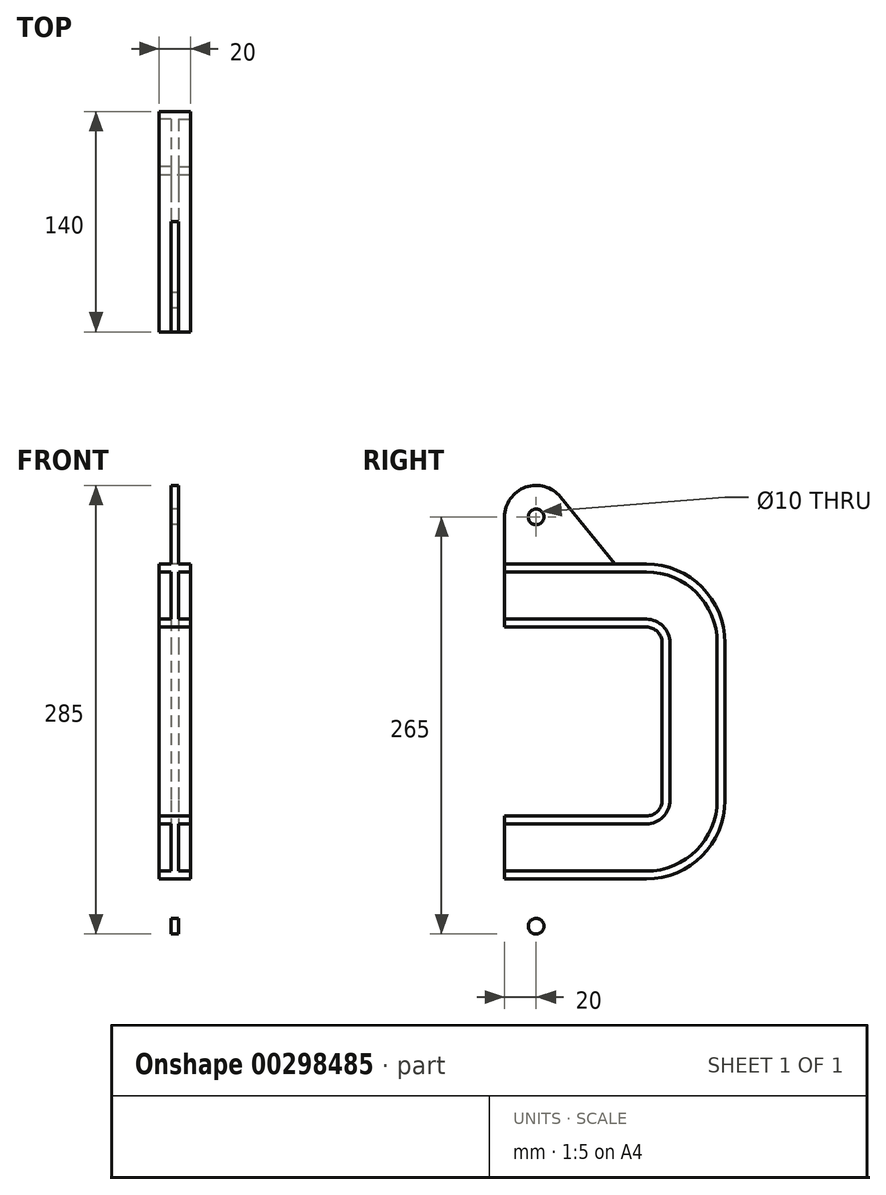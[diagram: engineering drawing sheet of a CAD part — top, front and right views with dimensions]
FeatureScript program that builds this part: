
annotation { "Feature Type Name" : "Feature", "Feature Type Description" : "" }
export const myFeature = defineFeature(function(context is Context, id is Id, definition is map)
    precondition{}
    {
        {
            var Q0;
            Q0=qCreatedBy(makeId("Front.planeOp"),FACE);
            var sketch = newSketch(context, id + "F0", { "sketchPlane" : qUnion([Q0])});
            skLineSegment(sketch, "E0", {"start": v(2.5, 0) * mm, "end": v(2.5, 15) * mm});
            skLineSegment(sketch, "E1", {"start": v(5.5, 15) * mm, "end": v(10, 15) * mm});
            skLineSegment(sketch, "E2", {"start": v(10, 15) * mm, "end": v(10, 20) * mm});
            skLineSegment(sketch, "E3", {"start": v(10, 20) * mm, "end": v(0, 20) * mm});
            skLineSegment(sketch, "E4.MirrorCS", {"start": v(-10, 15) * mm, "end": v(-10, 20) * mm});
            skLineSegment(sketch, "E5.MirrorCS", {"start": v(-2.5, 15) * mm, "end": v(-10, 15) * mm});
            skLineSegment(sketch, "E6.MirrorCS", {"start": v(-2.5, 0) * mm, "end": v(-2.5, 15) * mm});
            skLineSegment(sketch, "E7.MirrorCS", {"start": v(-10, 20) * mm, "end": v(0, 20) * mm});
            skLineSegment(sketch, "E8.MirrorCS", {"start": v(2.5, 0) * mm, "end": v(2.5, 12) * mm});
            skLineSegment(sketch, "E9.MirrorCS", {"start": v(-5.5, 15) * mm, "end": v(-10, 15) * mm});
            skLineSegment(sketch, "E10.MirrorCS", {"start": v(-2.5, 0) * mm, "end": v(-2.5, 12) * mm});
            skLineSegment(sketch, "E11.MirrorCS", {"start": v(2.5, 15) * mm, "end": v(10, 15) * mm});
            skLineSegment(sketch, "E12.MirrorCS", {"start": v(-10, -20) * mm, "end": v(0, -20) * mm});
            skLineSegment(sketch, "E13.MirrorCS", {"start": v(2.5, 0) * mm, "end": v(2.5, -15) * mm});
            skLineSegment(sketch, "E14.MirrorCS", {"start": v(5.5, -15) * mm, "end": v(10, -15) * mm});
            skLineSegment(sketch, "E15.MirrorCS", {"start": v(10, -15) * mm, "end": v(10, -20) * mm});
            skLineSegment(sketch, "E16.MirrorCS", {"start": v(-10, -15) * mm, "end": v(-10, -20) * mm});
            skLineSegment(sketch, "E17.MirrorCS", {"start": v(-2.5, 0) * mm, "end": v(-2.5, -15) * mm});
            skLineSegment(sketch, "E18.MirrorCS", {"start": v(-2.5, -15) * mm, "end": v(-10, -15) * mm});
            skLineSegment(sketch, "E19.MirrorCS", {"start": v(10, -20) * mm, "end": v(0, -20) * mm});
            skLineSegment(sketch, "E20.MirrorCS", {"start": v(2.5, -15) * mm, "end": v(10, -15) * mm});
            skLineSegment(sketch, "E21.MirrorCS", {"start": v(-2.5, 0) * mm, "end": v(-2.5, -12) * mm});
            skLineSegment(sketch, "E22.MirrorCS", {"start": v(-5.5, -15) * mm, "end": v(-10, -15) * mm});
            skLineSegment(sketch, "E23.MirrorCS", {"start": v(2.5, 0) * mm, "end": v(2.5, -12) * mm});
            skPoint(sketch, "E24.visualSharp", {"position": v(2.5, 15) * mm});
            skArc(sketch, "E24.filletArc", {"start": v(5.5, 15) * mm, "mid": v(3.38, 14.12) * mm, "end": v(2.5, 12) * mm});
            skPoint(sketch, "E25.visualSharp", {"position": v(-2.5, 15) * mm});
            skArc(sketch, "E25.filletArc", {"start": v(-2.5, 12) * mm, "mid": v(-3.38, 14.12) * mm, "end": v(-5.5, 15) * mm});
            skPoint(sketch, "E26.visualSharp", {"position": v(-2.5, -15) * mm});
            skArc(sketch, "E26.filletArc", {"start": v(-5.5, -15) * mm, "mid": v(-3.38, -14.12) * mm, "end": v(-2.5, -12) * mm});
            skPoint(sketch, "E27.visualSharp", {"position": v(2.5, -15) * mm});
            skArc(sketch, "E27.filletArc", {"start": v(2.5, -12) * mm, "mid": v(3.38, -14.12) * mm, "end": v(5.5, -15) * mm});
            skSolve(sketch);
        }
        {
            var Q0;
            Q0=qCreatedBy(makeId("Right.planeOp"),FACE);
            var sketch = newSketch(context, id + "F1", { "sketchPlane" : qUnion([Q0])});
            skLineSegment(sketch, "E28", {"start": v(0, -20) * mm, "end": v(90, -20) * mm});
            skLineSegment(sketch, "E29", {"start": v(100, -130) * mm, "end": v(100, -30) * mm});
            skLineSegment(sketch, "E30", {"start": v(90, -140) * mm, "end": v(0, -140) * mm});
            skPoint(sketch, "E31.visualSharp", {"position": v(100, -20) * mm});
            skArc(sketch, "E31.filletArc", {"start": v(100, -30) * mm, "mid": v(97.07, -22.93) * mm, "end": v(90, -20) * mm});
            skPoint(sketch, "E32.visualSharp", {"position": v(100, -140) * mm});
            skArc(sketch, "E32.filletArc", {"start": v(90, -140) * mm, "mid": v(97.07, -137.07) * mm, "end": v(100, -130) * mm});
            skSolve(sketch);
        }
        {
            var Q0;
            {var subQ4=sQuery(id+"F0.wireOp",EDGE,"E0");Q0=makeQuery(id+"F0.imprint","IMPRINT",FACE,{"disambiguationData":[TD([[makeQuery(id+"F0.imprint","IMPRINT",EDGE,{"derivedFrom":subQ4}),1.0]])]});}
            var Q1;
            Q1=sQuery(id+"F1.wireOp",EDGE,"E28");
            var Q2;
            Q2=sQuery(id+"F1.wireOp",EDGE,"E31.filletArc");
            var Q3;
            Q3=sQuery(id+"F1.wireOp",EDGE,"E29");
            var Q4;
            Q4=sQuery(id+"F1.wireOp",EDGE,"E32.filletArc");
            var Q5;
            Q5=sQuery(id+"F1.wireOp",EDGE,"E30");
            sweep(context, id + "F2", {"profiles" : qUnion([Q0]), "path" : qUnion([Q1, Q2, Q3, Q4, Q5])});
        }
        {
            var Q0;
            Q0=qCreatedBy(makeId("Right.planeOp"),FACE);
            var sketch = newSketch(context, id + "F3", { "sketchPlane" : qUnion([Q0])});
            skLineSegment(sketch, "E33", {"start": v(0, 20) * mm, "end": v(70, 20) * mm});
            skLineSegment(sketch, "E34", {"start": v(70, 20) * mm, "end": v(35.55, 62.58) * mm});
            skArc(sketch, "E35", {"start": v(35.55, 62.58) * mm, "mid": v(13.33, 68.85) * mm, "end": v(0, 50) * mm});
            skLineSegment(sketch, "E36", {"start": v(0, 50) * mm, "end": v(0, 20) * mm});
            skCircle(sketch, "E37", {"center": v(20, 50) * mm, "radius": 5 * mm});
            skLineSegment(sketch, "E38", {"start": v(33.98, -80) * mm, "end": v(186, -80) * mm, "construction": true});
            skCircle(sketch, "E39.MirrorC", {"center": v(20, -210) * mm, "radius": 5 * mm});
            skLineSegment(sketch, "E40.MirrorCS", {"start": v(0, -210) * mm, "end": v(0, -180) * mm});
            skArc(sketch, "E41.MirrorCS", {"start": v(35.55, -222.58) * mm, "mid": v(13.33, -228.85) * mm, "end": v(0, -210) * mm});
            skLineSegment(sketch, "E42.MirrorCS", {"start": v(0, -180) * mm, "end": v(70, -180) * mm});
            skLineSegment(sketch, "E43.MirrorCS", {"start": v(70, -180) * mm, "end": v(35.55, -222.58) * mm});
            skSolve(sketch);
        }
        {
            var Q0;
            Q0=makeQuery(id+"F3.imprint","IMPRINT",FACE,{"disambiguationData":[TD([[makeQuery(id+"F3.imprint","IMPRINT",EDGE,{"derivedFrom":sQuery(id+"F3.wireOp",EDGE,"E33")}),1.0]])]});
            var Q1;
            Q1=makeQuery(id+"F3.imprint","IMPRINT",FACE,{"disambiguationData":[TD([[makeQuery(id+"F3.imprint","IMPRINT",EDGE,{"derivedFrom":sQuery(id+"F3.wireOp",EDGE,"E39.MirrorC")}),1.0]])]});
            extrude(context, id + "F4", {"entities" : qUnion([Q0, Q1]), "operationType" : NewBodyOperationType.ADD, "endBound" : BoundingType.SYMMETRIC, "depth" : 5 * mm});
        }
    });
